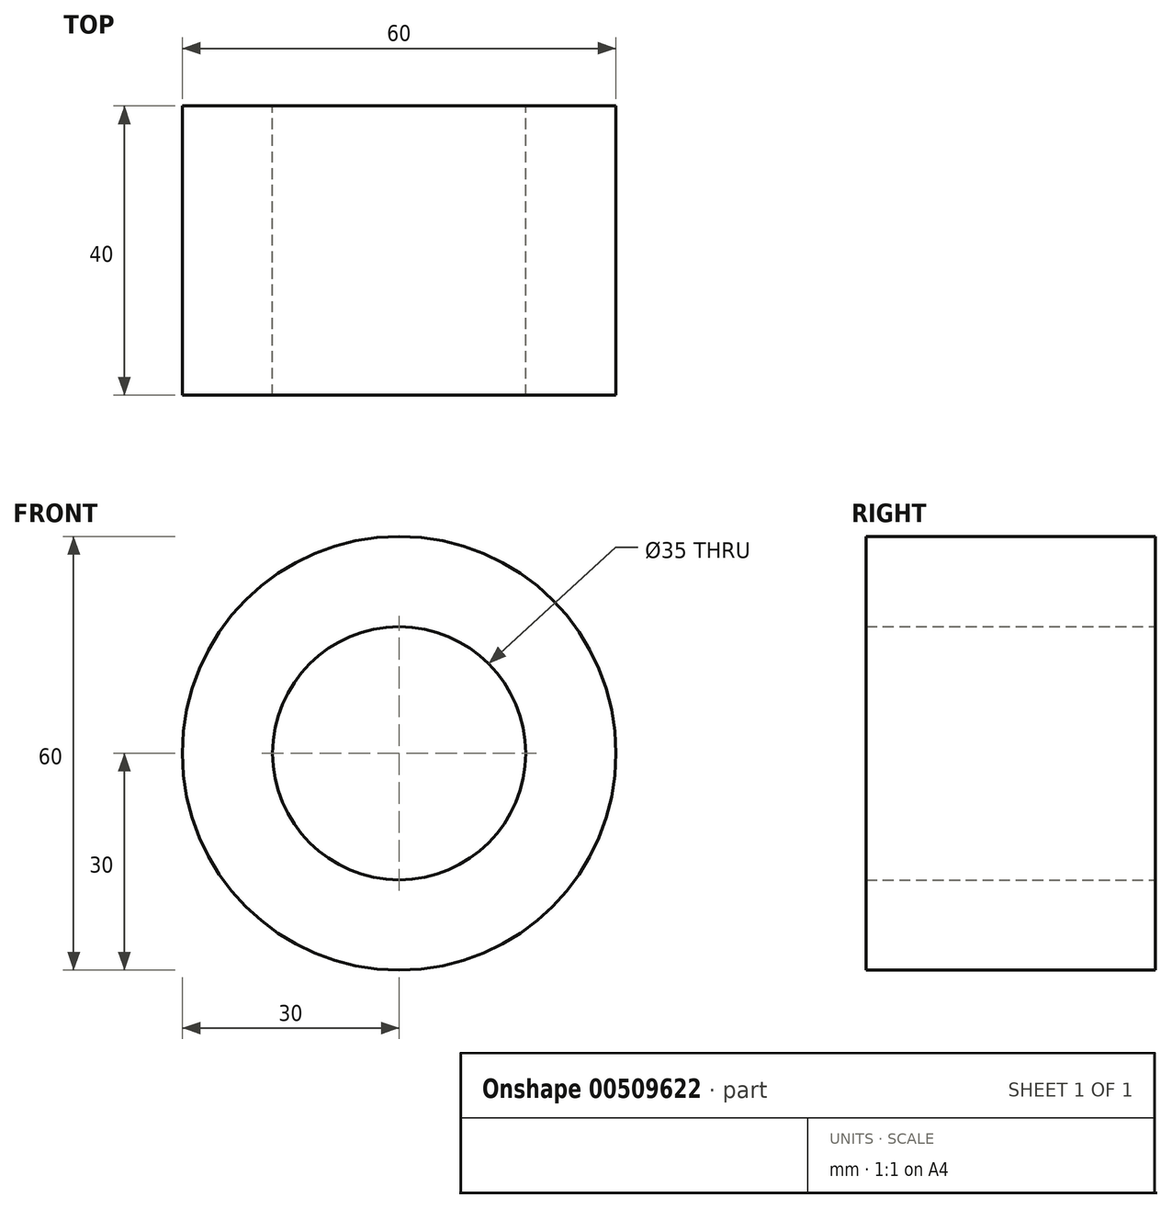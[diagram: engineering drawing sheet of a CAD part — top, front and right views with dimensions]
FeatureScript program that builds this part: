
annotation { "Feature Type Name" : "Feature", "Feature Type Description" : "" }
export const myFeature = defineFeature(function(context is Context, id is Id, definition is map)
    precondition{}
    {
        {
            var Q0;
            Q0=qCreatedBy(makeId("Front.planeOp"),FACE);
            var sketch = newSketch(context, id + "F0", { "sketchPlane" : qUnion([Q0])});
            skCircle(sketch, "E0", {"center": v(0, 0) * mm, "radius": 17.5 * mm});
            skCircle(sketch, "E1", {"center": v(0, 0) * mm, "radius": 30 * mm});
            skSolve(sketch);
        }
        {
            var Q0;
            Q0=makeQuery(id+"F0.imprint","IMPRINT",FACE,{"disambiguationData":[TD([[makeQuery(id+"F0.imprint","IMPRINT",EDGE,{"derivedFrom":sQuery(id+"F0.wireOp",EDGE,"E0")}),-1.0]])]});
            extrude(context, id + "F1", {"entities" : qUnion([Q0]), "endBound" : BoundingType.SYMMETRIC, "depth" : 40 * mm});
        }
    });
